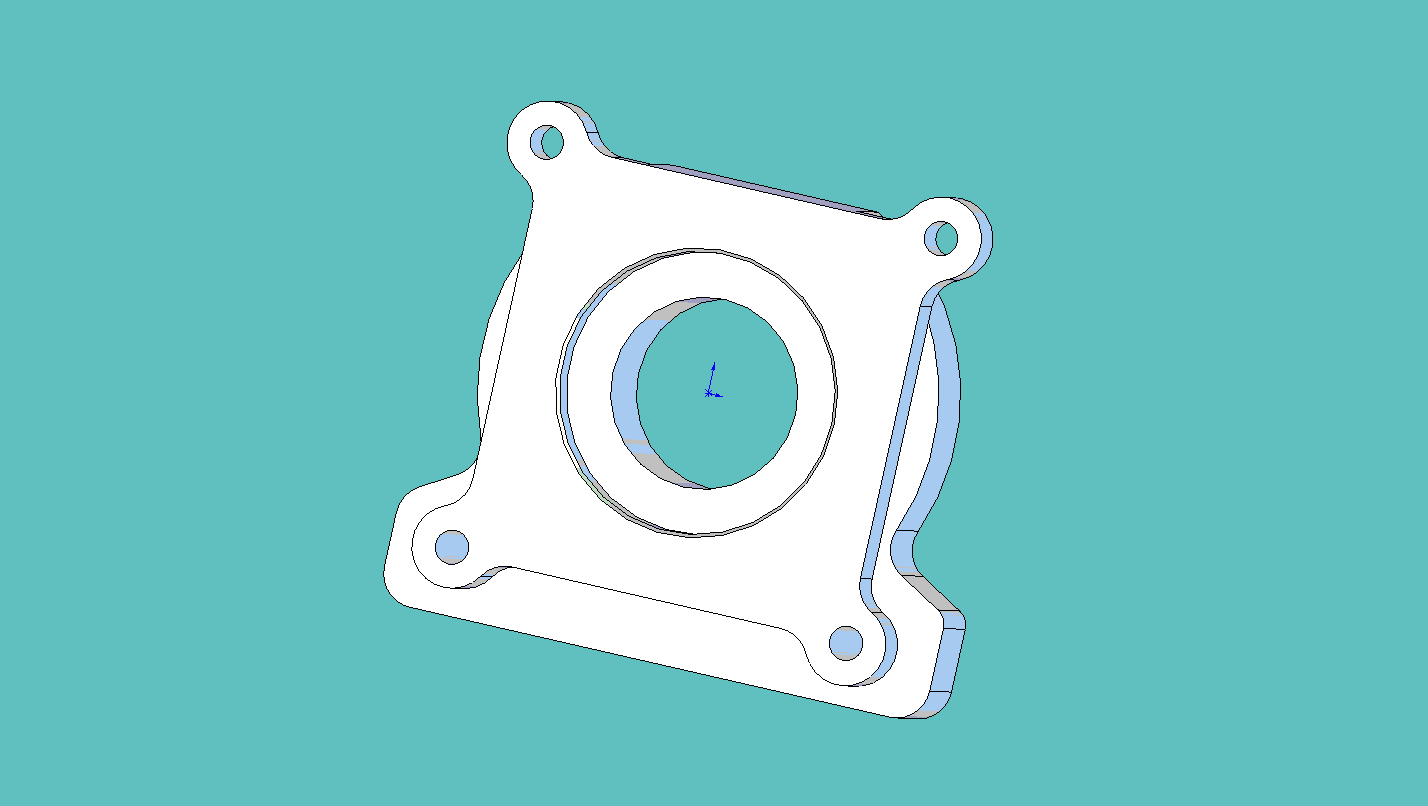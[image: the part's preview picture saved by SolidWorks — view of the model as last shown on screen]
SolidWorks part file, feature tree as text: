
SOLIDWORKS PART (.sldprt)
format: sldprt  version: not decoded by parser v0  size: 395,776 bytes
history: native  units: mm
features: sketch x6, cut_extrude x4, extrude x2, material x1, fillet x1, chamfer x1 (+13 scaffold rows collapsed)
feature tree (28):
  scaffold x13  (default folders/planes/origin — collapsed)
  material  "Material <not specified>"
  sketch  "Sketch1"  dims[D1=12.7mm D2=~122.851231mm]
  extrude  "Extrude1"  Depth=19.05mm
  fillet  "Fillet1"  Radius=12.7mm
  sketch  "Sketch2"  dims[D1=~104.655842mm D2=~104.667819mm]
  cut_extrude  "Cut-Extrude2"  Depth=12.7mm
  chamfer  "Chamfer1"  Distance=1.27mm Angle=45deg
  sketch  "Sketch4"  dims[D1=12.7mm D2=12.7mm]
  extrude  "Extrude2"  Depth=35.56mm
  sketch  "Sketch3"  dims[D1=71.12mm]
  cut_extrude  "Cut-Extrude3"  [1 undecoded]
  sketch  "Sketch5"
  cut_extrude  "Cut-Extrude4"  Depth=40.64mm
  sketch  "Sketch7"
  cut_extrude  "Cut-Extrude6"  [1 undecoded]
decode coverage: 10 of 14 modeling features carry decoded parameters
note: ~ marks probable driven/reference dimensions
note: 2 parameter values undecoded
note: suppression state not decoded; provenance and decode notes live in map.json
